# Revit family: CONV_Wexiodisk_Dishwasher_WD-7
name_source: partatom
category: Specialty Equipment
revit_build: Autodesk Revit 2016 (Build: 20150714_1515(x64)
units: mm (PartAtom-declared; Revit-internal decimal feet)

## family parameters
Always vertical = Yes
Cut with Voids When Loaded = No
OmniClass Number = 23.45.30.14.11
OmniClass Title = Commercial Dishwashers
Part Type = Normal
Room Calculation Point = No
Round Connector Dimension = Use Diameter
Shared = No
Work Plane-Based = No

## types (1)
- WD-7
    AssetType = Fixed
    BIMObjectName = CONV_Wexiodisk_Dishwasher_WD-7
    BasketSize = 500x500mm
    BoosterHeater = 9000 W
    Brand = Wexiodisk
    CapacityBasketsPerHour = 50
    Category = Hood type dishwashing machines
    Color = Grey
    ConvergoRefNr = 0100-1703-0004-SE
    Cost = 0 $
    DishwasherMainMaterial = Stainless Steel
    DishwasherSecondaryMaterial = Black Plastic
    DrainConnectionHose = 50.00 mm
    DurationUnit = Year
    ElectricalDeviceNominalPower = 0 W
    ExpiringDate = 12/2018
    Features = Alternative water connection from below,Water outlet for detergent, Plugged hole for detergent hose
    FloorDrain = 3.0 L/s
    HasProtectiveEarth = No
    HeatLoadToRoomLatent = 600 W
    HeatLoadToRoomSensible = 1700 W
    HeatLoadToRoomTotal = 2300 W
    IP_Code = 45
    IfcExportAs = NOTDEFINED
    IfcExportType = IfcFurnitureType
    MainFuse(400V-3N) = 16 A
    ManufacterURL = https://www.wexiodisk.com
    Manufacturer = Wexiodisk
    ManufacturerName = Wexiodisk
    Material = Stainless Steel
    Model = WD-7
    NBSDescription = Commercial passthrough dishwashers
    NBSReference = 45-35-15/422
    Name = Dishwasher_WD7
    NominalCurrent = 0 A
    NominalDepth = 720 mm  [stored 2.3622 ft]
    NominalFrequencyRange = 0 Hz
    NominalHeight = 1540 mm  [stored 5.05249 ft]
    NominalVoltage = 400 V
    NominalWidth = 755 mm  [stored 2.47703 ft]
    NumberOfPoles = 0
    PhaseAngle = 0.00°
    Revision = 2
    Shape = Cube
    Size = 720x755x1540mm
    SoundLevel = 60 dB
    TankHeater = 1800 W
    TankVolume = 50.0 L
    URL = https://www.wexiodisk.com
    Uniclass2 = Pr_40_70_21_60
    Uniclass2015Description = Pass-through dishwashers
    Uniclass2015Reference = Pr_40_70_21_60
    UsageCurrent = 0 A
    Version = 2
    VersionDate = 01/01/2018
    WarrantyDurationUnit = Year
    WashPump = 1100 W
    WaterCapacityFlow = 0.3 L/s
    WaterCapacityHoodLiftPressure = 300000.0 Pa
    WaterCapacityPressure = 180000.0 Pa
    WaterConnection(5-70°) = R1/2"
    WaterConsumptionRinse/Programme = 4.0 L
    WaterQuality = 2-7 °dH
    WeightMachineInOperation = 170kg

note: [stored X ft] marks values corroborated as IEEE doubles in the binary element streams (Revit-internal decimal feet)

## geometry (parser evidence)
native form markers: Blend x4, Sweep x2
no freeform markers — native parametric forms only
